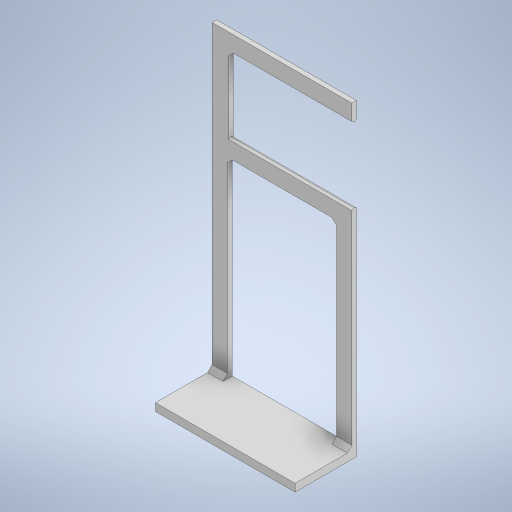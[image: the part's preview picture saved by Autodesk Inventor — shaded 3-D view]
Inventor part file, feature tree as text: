
AUTODESK INVENTOR PART (.ipt)
format: ipt  version: 2023.2 (Build 272271000, 271)  size: 300,032 bytes
history: native  units: mm
features: extrude x4, sketch x4, chamfer x2
ambient origin geometry x8: Origin, YZ Plane, XZ Plane, XY Plane, X Axis, Y Axis, Z Axis, Center Point
bodies: Volumenkörper1 (feature_tree)
feature tree (10):
  extrude  "Extrusion1"  Depth=71.0mm
  extrude  "Extrusion2"  Depth=80.3mm
  extrude  "Extrusion3"  TaperAngle=30.0deg  [1 undecoded]
  chamfer  "Fase1"  Distance=3.0mm
  extrude  "Extrusion5"  Depth=10.0mm
  chamfer  "Fase2"  Distance=130.0mm
  sketch  "Skizze1"  dims[d0=91.0mm d1=71.0mm]
  sketch  "Skizze3"  dims[d2=3.0mm d3=0.0mm d4=80.3mm]
  sketch  "Skizze4"  dims[d5=50.3mm d7=30.0deg d8=3.0mm d9=0.0mm]
  sketch  "Skizze6"  dims[d10=10.0mm d11=10.0mm d12=130.0mm d13=0.0mm d14=3.0mm d15=2.0mm d16=45.0deg d20=5.0mm d21=40.0mm d22=0.0mm d23=135.0deg d24=3.0mm d25=3.0mm d26=2.0mm d27=45.0deg]
note: 1 required parameter value undecoded (feature->parameter linkage not recoverable at this tier; creation-order binding heuristic only, values carry confidence <= 0.55)
